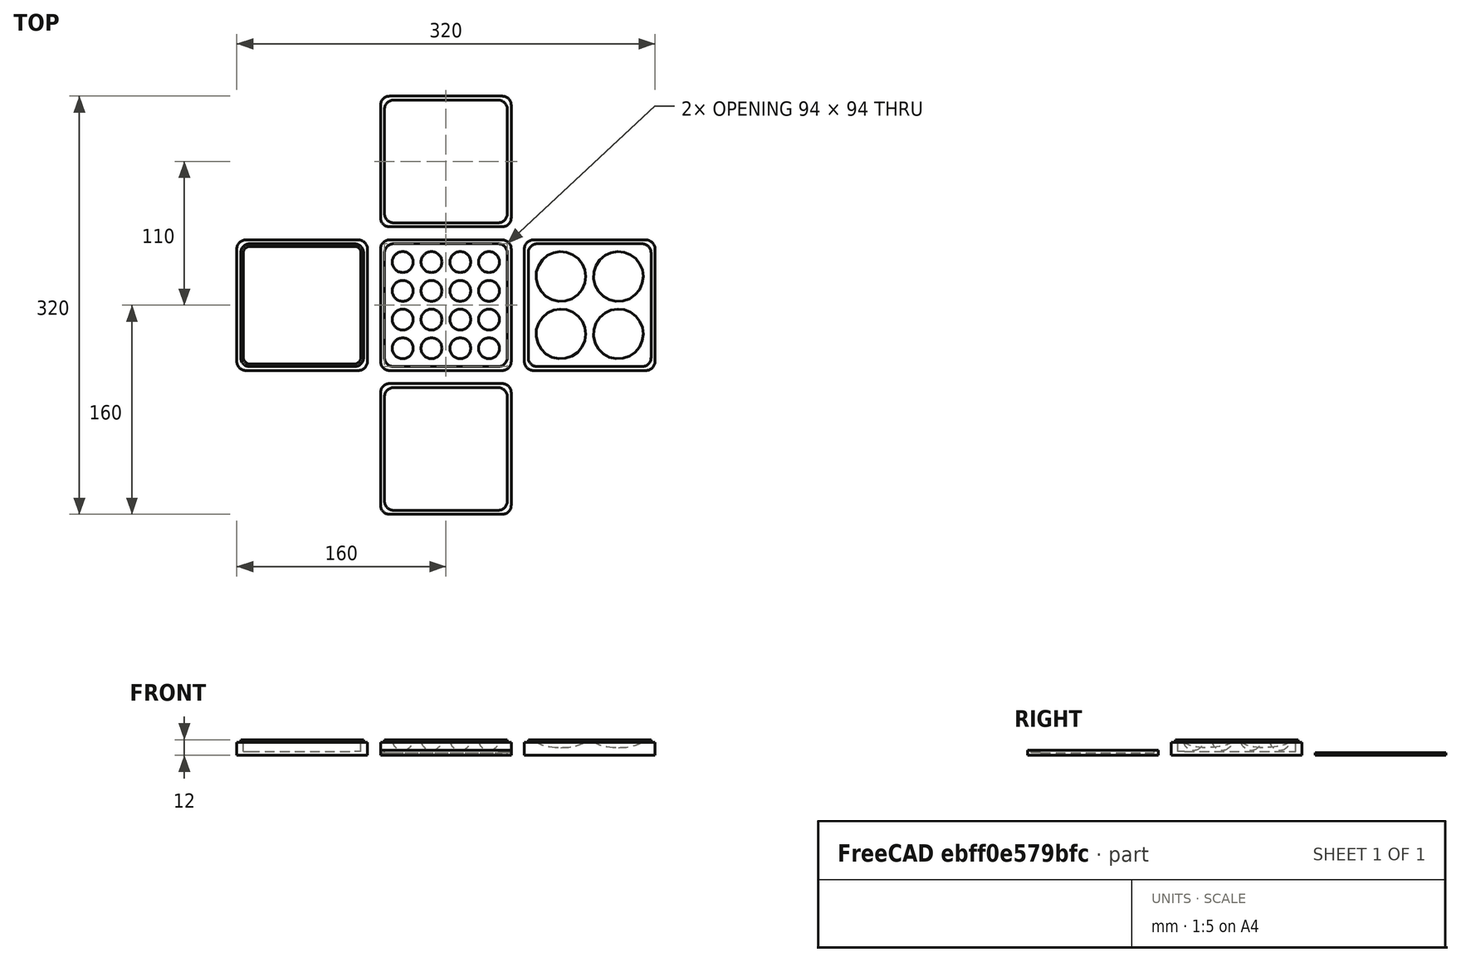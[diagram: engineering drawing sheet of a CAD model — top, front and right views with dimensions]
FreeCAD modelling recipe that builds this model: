
FCSTD DOCUMENT  (FreeCAD 0.18R16146 (Git))
Label: palette
License: All rights reserved
LicenseURL: http://en.wikipedia.org/wiki/All_rights_reserved
objects: Part::Box×13, Part::Fillet×13, Part::Cut×5, Part::MultiFuse×4, Part::FeaturePython×2, Part::Sphere×1, Part::Ellipsoid×1
note: 39 computed .brp shape members not serialized (recipe doc carries the construction recipe); baked Part::Feature solids carry a one-line shape summary decoded from their .brp

FEATURE [Part::Box] Box  label="Body"
  AttacherType = Attacher::AttachEngine3D
  Height = 10
  Length = 100
  Width = 100
FEATURE [Part::Fillet] Fillet  label="Body with fillets"
  Base = -> Box
  Edges = 4 edges r=7: [Edge1,Edge3,Edge5,Edge7]
FEATURE [Part::Box] Box001  label="Top"
  AttacherType = Attacher::AttachEngine3D
  Height = 2
  Length = 94
  Placement = pos=(3,3,10) rot=(0,0,1;0rad)
  Width = 94
FEATURE [Part::Fillet] Fillet001  label="Top with fillets"
  Base = -> Box001
  Edges = 4 edges r=7: [Edge1,Edge3,Edge5,Edge7]
FEATURE [Part::MultiFuse] Fusion  label="Base"
  Shapes = -> [Fillet001,Fillet]
FEATURE [Part::Box] Box002  label="Body001"
  AttacherType = Attacher::AttachEngine3D
  Height = 10
  Length = 100
  Width = 100
FEATURE [Part::Box] Box003  label="Top001"
  AttacherType = Attacher::AttachEngine3D
  Height = 2
  Length = 94
  Placement = pos=(3,3,10) rot=(0,0,1;0rad)
  Width = 94
FEATURE [Part::Fillet] Fillet002  label="Body with fillets001"
  Base = -> Box002
  Edges = 4 edges r=7: [Edge1,Edge3,Edge5,Edge7]
FEATURE [Part::Fillet] Fillet003  label="Top with fillets001"
  Base = -> Box003
  Edges = 4 edges r=7: [Edge1,Edge3,Edge5,Edge7]
FEATURE [Part::MultiFuse] Fusion001  label="Base003"
  Shapes = -> [Fillet003,Fillet002]
FEATURE [Part::Sphere] Sphere  label="Sphère"
  Angle1 = -90
  Angle2 = 90
  Angle3 = 360
  AttacherType = Attacher::AttachEngine3D
  Placement = pos=(17,17,12) rot=(0,0,1;0rad)
  Radius = 8
FEATURE [Part::FeaturePython] Array  # Draft array (typed FeaturePython)
  Angle = 360
  ArrayType = 0
  Axis = (0,0,1)
  Base = -> Sphere
  Center = (0,0,0)
  Fuse = false
  IntervalAxis = (0,0,0)
  IntervalX = (22,0,0)
  IntervalY = (0,22,0)
  IntervalZ = (0,0,0)
  NumberPolar = 1
  NumberX = 4
  NumberY = 4
  NumberZ = 1
FEATURE [Part::Cut] Cut  label="Well Palette"
  Base = -> Fusion
  Tool = -> Array
FEATURE [Part::Box] Box004  label="Body002"
  AttacherType = Attacher::AttachEngine3D
  Height = 10
  Length = 100
  Width = 100
FEATURE [Part::Fillet] Fillet005  label="Body with fillets002"
  Base = -> Box004
  Edges = 4 edges r=7: [Edge1,Edge3,Edge5,Edge7]
FEATURE [Part::Box] Box005  label="Top002"
  AttacherType = Attacher::AttachEngine3D
  Height = 2
  Length = 94
  Placement = pos=(3,3,10) rot=(0,0,1;0rad)
  Width = 94
FEATURE [Part::Fillet] Fillet004  label="Top with fillets002"
  Base = -> Box005
  Edges = 4 edges r=7: [Edge1,Edge3,Edge5,Edge7]
FEATURE [Part::MultiFuse] Fusion002  label="Base002"
  Shapes = -> [Fillet004,Fillet005]
FEATURE [Part::Ellipsoid] Ellipsoid  label="Ellipsoïde"
  Angle1 = -90
  Angle2 = 90
  Angle3 = 360
  AttacherType = Attacher::AttachEngine3D
  Placement = pos=(28,28,12) rot=(0,0,1;0rad)
  Radius1 = 6
  Radius2 = 19
  Radius3 = 19
FEATURE [Part::FeaturePython] Array001  # Draft array (typed FeaturePython)
  Angle = 360
  ArrayType = 0
  Axis = (0,0,1)
  Base = -> Ellipsoid
  Center = (0,0,0)
  Fuse = false
  IntervalAxis = (0,0,0)
  IntervalX = (44,0,0)
  IntervalY = (0,44,0)
  IntervalZ = (0,0,0)
  NumberPolar = 1
  NumberX = 2
  NumberY = 2
  NumberZ = 1
FEATURE [Part::Cut] Cut001  label="Washes Palette"
  Base = -> Fusion002
  Placement = pos=(110,0,0) rot=(0,0,1;0rad)
  Tool = -> Array001
FEATURE [Part::Box] Box006  label="Cube"
  AttacherType = Attacher::AttachEngine3D
  Height = 10
  Length = 90
  Placement = pos=(5,5,3) rot=(0,0,1;0rad)
  Width = 90
FEATURE [Part::Box] Box007  label="Body003"
  AttacherType = Attacher::AttachEngine3D
  Height = 10
  Length = 100
  Width = 100
FEATURE [Part::Fillet] Fillet007  label="Body with fillets003"
  Base = -> Box007
  Edges = 4 edges r=7: [Edge1,Edge3,Edge5,Edge7]
FEATURE [Part::Box] Box008  label="Top003"
  AttacherType = Attacher::AttachEngine3D
  Height = 2
  Length = 94
  Placement = pos=(3,3,10) rot=(0,0,1;0rad)
  Width = 94
FEATURE [Part::Fillet] Fillet006  label="Top with fillets003"
  Base = -> Box008
  Edges = 4 edges r=7: [Edge1,Edge3,Edge5,Edge7]
FEATURE [Part::MultiFuse] Fusion003  label="Base004"
  Shapes = -> [Fillet006,Fillet007]
FEATURE [Part::Fillet] Fillet008
  Base = -> Box006
  Edges = 4 edges r=5: [Edge1,Edge3,Edge5,Edge7]
FEATURE [Part::Cut] Cut002  label="Wet Palette"
  Base = -> Fusion003
  Placement = pos=(-110,0,0) rot=(0,0,1;0rad)
  Tool = -> Fillet008
FEATURE [Part::Box] Box009  label="Body004"
  AttacherType = Attacher::AttachEngine3D
  Height = 2
  Length = 100
  Width = 100
FEATURE [Part::Fillet] Fillet010  label="Body with fillets004"
  Base = -> Box009
  Edges = 4 edges r=7: [Edge1,Edge3,Edge5,Edge7]
FEATURE [Part::Box] Box010  label="Top004"
  AttacherType = Attacher::AttachEngine3D
  Height = 2
  Length = 94
  Placement = pos=(3,3,0) rot=(0,0,1;0rad)
  Width = 94
FEATURE [Part::Fillet] Fillet011  label="Top with fillets004"
  Base = -> Box010
  Edges = 4 edges r=7: [Edge1,Edge3,Edge5,Edge7]
FEATURE [Part::Cut] Cut003  label="Stacker"
  Base = -> Fillet010
  Placement = pos=(0,110,0) rot=(0,0,1;0rad)
  Tool = -> Fillet011
FEATURE [Part::Box] Box011  label="Body005"
  AttacherType = Attacher::AttachEngine3D
  Height = 4
  Length = 100
  Width = 100
FEATURE [Part::Fillet] Fillet012  label="Body with fillets005"
  Base = -> Box011
  Edges = 4 edges r=7: [Edge1,Edge3,Edge5,Edge7]
FEATURE [Part::Box] Box012  label="Top005"
  AttacherType = Attacher::AttachEngine3D
  Height = 2
  Length = 94
  Placement = pos=(3,3,2) rot=(0,0,1;0rad)
  Width = 94
FEATURE [Part::Fillet] Fillet013  label="Top with fillets005"
  Base = -> Box012
  Edges = 4 edges r=7: [Edge1,Edge3,Edge5,Edge7]
FEATURE [Part::Cut] Cut004  label="Lid"
  Base = -> Fillet012
  Placement = pos=(0,-110,0) rot=(0,0,1;0rad)
  Tool = -> Fillet013
